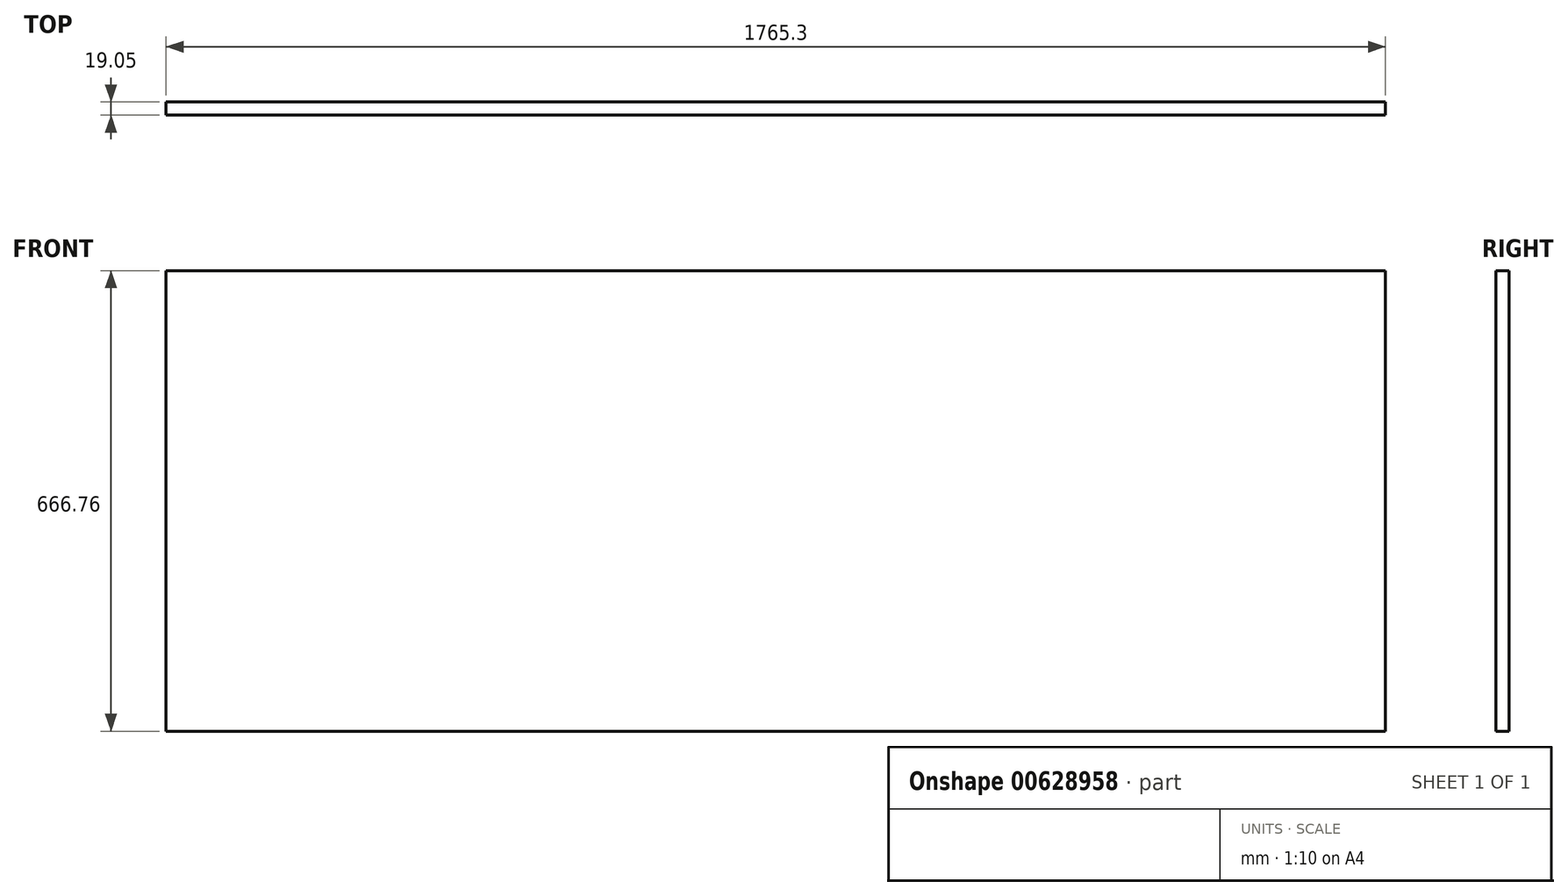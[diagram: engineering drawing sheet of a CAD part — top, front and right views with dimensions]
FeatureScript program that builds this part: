
annotation { "Feature Type Name" : "Feature", "Feature Type Description" : "" }
export const myFeature = defineFeature(function(context is Context, id is Id, definition is map)
    precondition{}
    {
        {
            var Q0;
            Q0=qCreatedBy(makeId("Front.planeOp"),FACE);
            var sketch = newSketch(context, id + "F0", { "sketchPlane" : qUnion([Q0])});
            skLineSegment(sketch, "E0.bottom", {"start": v(-882.65, 333.38) * mm, "end": v(882.65, 333.38) * mm});
            skLineSegment(sketch, "E0.top", {"start": v(-882.65, -333.38) * mm, "end": v(882.65, -333.38) * mm});
            skLineSegment(sketch, "E0.left", {"start": v(-882.65, 333.38) * mm, "end": v(-882.65, -333.38) * mm});
            skLineSegment(sketch, "E0.right", {"start": v(882.65, 333.38) * mm, "end": v(882.65, -333.38) * mm});
            skPoint(sketch, "E0.middle", {"position": v(0, 0) * mm});
            skSolve(sketch);
        }
        {
            var Q0;
            Q0=makeQuery(id+"F0.imprint","IMPRINT",FACE,{"disambiguationData":[TD([[makeQuery(id+"F0.imprint","IMPRINT",EDGE,{"derivedFrom":sQuery(id+"F0.wireOp",EDGE,"E0.bottom")}),-1.0]])]});
            extrude(context, id + "F1", {"entities" : qUnion([Q0]), "depth" : 19.05 * mm, "offsetDistance" : 25.4 * mm});
        }
    });
